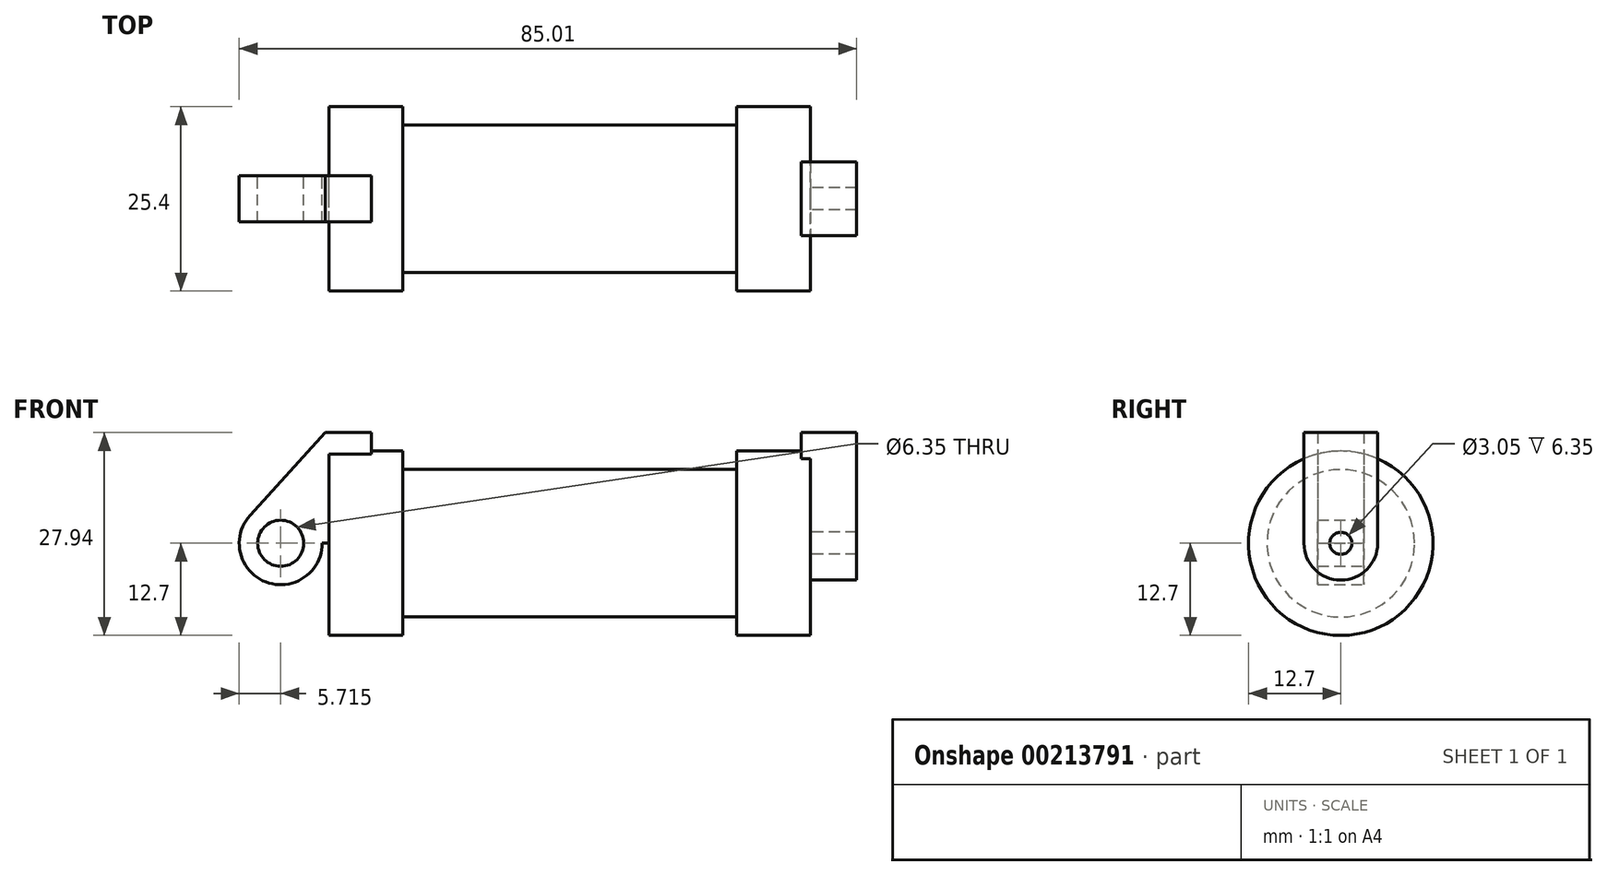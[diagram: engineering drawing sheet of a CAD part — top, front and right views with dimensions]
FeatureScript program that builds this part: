
annotation { "Feature Type Name" : "Feature", "Feature Type Description" : "" }
export const myFeature = defineFeature(function(context is Context, id is Id, definition is map)
    precondition{}
    {
        {
            var Q0;
            Q0=qCreatedBy(makeId("Front.planeOp"),FACE);
            var sketch = newSketch(context, id + "F0", { "sketchPlane" : qUnion([Q0])});
            skLineSegment(sketch, "E0", {"start": v(0, 0) * mm, "end": v(0, 12.7) * mm});
            skLineSegment(sketch, "E1", {"start": v(0, 12.7) * mm, "end": v(10.16, 12.7) * mm});
            skLineSegment(sketch, "E2", {"start": v(10.16, 12.7) * mm, "end": v(10.16, 10.16) * mm});
            skLineSegment(sketch, "E3", {"start": v(10.16, 10.16) * mm, "end": v(56.13, 10.16) * mm});
            skLineSegment(sketch, "E4", {"start": v(56.13, 10.16) * mm, "end": v(56.13, 12.7) * mm});
            skLineSegment(sketch, "E5", {"start": v(56.13, 12.7) * mm, "end": v(66.3, 12.7) * mm});
            skLineSegment(sketch, "E6", {"start": v(66.3, 12.7) * mm, "end": v(66.3, 0) * mm});
            skLineSegment(sketch, "E7", {"start": v(66.3, 0) * mm, "end": v(0, 0) * mm});
            skLineSegment(sketch, "E8", {"start": v(5.84, 15.24) * mm, "end": v(-0.5, 15.24) * mm});
            skLineSegment(sketch, "E9", {"start": v(-0.5, 15.24) * mm, "end": v(-10.88, 3.85) * mm});
            skLineSegment(sketch, "E10", {"start": v(0, 0) * mm, "end": v(-6.65, 0) * mm});
            skCircle(sketch, "E11", {"center": v(-6.65, 0) * mm, "radius": 5.72 * mm});
            skCircle(sketch, "E12", {"center": v(-6.65, 0) * mm, "radius": 3.18 * mm});
            skLineSegment(sketch, "E13", {"start": v(5.84, 15.24) * mm, "end": v(5.84, -9.4) * mm});
            skLineSegment(sketch, "E14", {"start": v(5.84, -9.4) * mm, "end": v(-8.18, -5.5) * mm});
            skSolve(sketch);
        }
        {
            var Q0;
            {var subQ0=sQuery(id+"F0.wireOp",EDGE,"E2");Q0=makeQuery(id+"F0.imprint","IMPRINT",FACE,{"disambiguationData":[TD([[makeQuery(id+"F0.imprint","IMPRINT",EDGE,{"derivedFrom":subQ0}),-1.0]])]});}
            var Q1;
            {var subQ0=sQuery(id+"F0.wireOp",EDGE,"E0");Q1=makeQuery(id+"F0.imprint","IMPRINT",FACE,{"disambiguationData":[TD([[makeQuery(id+"F0.imprint","IMPRINT",EDGE,{"derivedFrom":subQ0}),-1.0]])]});}
            var Q2;
            Q2=sQuery(id+"F0.wireOp",EDGE,"E7");
            revolve(context, id + "F1", {"entities" : qUnion([Q0, Q1]), "axis" : qUnion([Q2]), "revolveType" : RevolveType.FULL});
        }
        {
            var Q0;
            {var subQ0=sQuery(id+"F0.wireOp",EDGE,"E0");Q0=makeQuery(id+"F0.imprint","IMPRINT",FACE,{"disambiguationData":[TD([[makeQuery(id+"F0.imprint","IMPRINT",EDGE,{"derivedFrom":subQ0}),-1.0]])]});}
            var Q1;
            {var subQ3=sQuery(id+"F0.wireOp",EDGE,"E0");Q1=makeQuery(id+"F0.imprint","IMPRINT",FACE,{"disambiguationData":[TD([[makeQuery(id+"F0.imprint","IMPRINT",EDGE,{"derivedFrom":subQ3}),1.0]])]});}
            var Q2;
            {var subQ4=sQuery(id+"F0.wireOp",EDGE,"E12");Q2=makeQuery(id+"F0.imprint","IMPRINT",FACE,{"disambiguationData":[TD([[makeQuery(id+"F0.imprint","IMPRINT",EDGE,{"derivedFrom":subQ4}),-1.0]])]});}
            extrude(context, id + "F2", {"entities" : qUnion([Q0, Q1, Q2]), "operationType" : NewBodyOperationType.ADD, "endBound" : BoundingType.SYMMETRIC, "depth" : 6.35 * mm});
        }
        {
            var Q0;
            Q0=makeQuery(id+"F1.opRevolve","SWEPT_FACE",FACE,{"disambiguationData":[OSD([sQuery(id+"F0.wireOp",EDGE,"E6")])]});
            var sketch = newSketch(context, id + "F3", { "sketchPlane" : qUnion([Q0])});
            skCircle(sketch, "E15", {"center": v(0, 0) * mm, "radius": 1.52 * mm});
            skCircle(sketch, "E16", {"center": v(0, 0) * mm, "radius": 5.08 * mm});
            skLineSegment(sketch, "E17", {"start": v(5.08, 0) * mm, "end": v(5.08, 15.24) * mm});
            skLineSegment(sketch, "E18", {"start": v(5.08, 15.24) * mm, "end": v(-5.08, 15.24) * mm});
            skLineSegment(sketch, "E19", {"start": v(-5.08, 15.24) * mm, "end": v(-5.08, 0) * mm});
            skSolve(sketch);
        }
        {
            var Q0;
            Q0 = qSketchRegion(id + "F3", true);
            extrude(context, id + "F4", {"entities" : qUnion([Q0]), "operationType" : NewBodyOperationType.ADD, "depth" : 6.35 * mm, "hasSecondDirection" : true, "secondDirectionOppositeDirection" : true, "secondDirectionDepth" : 1.27 * mm});
        }
    });
